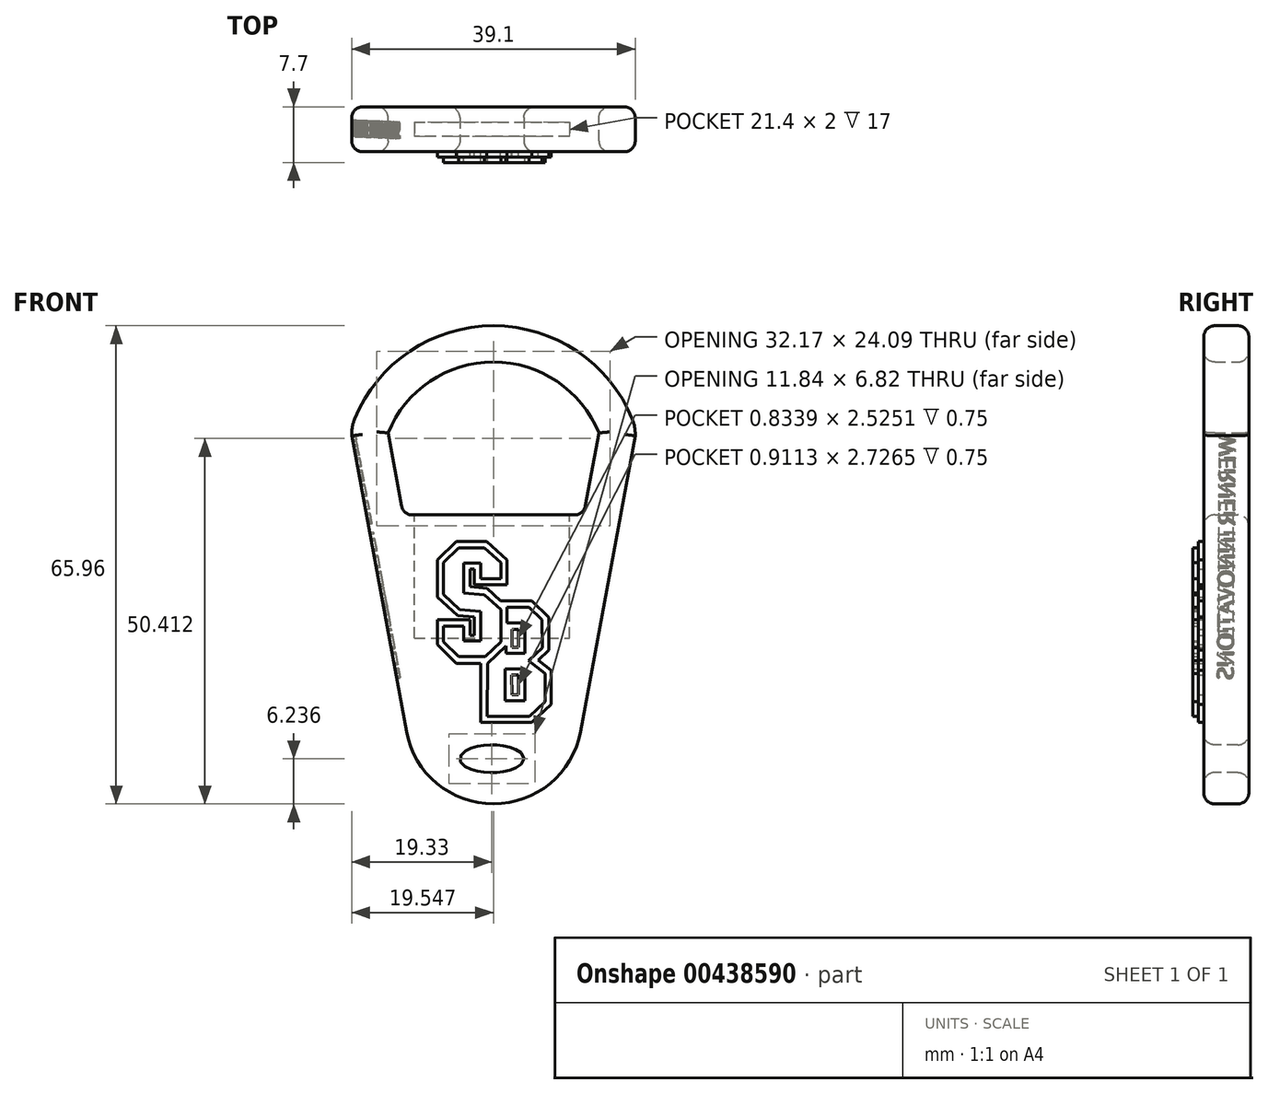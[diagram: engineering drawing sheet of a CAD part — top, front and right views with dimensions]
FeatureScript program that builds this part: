
annotation { "Feature Type Name" : "Feature", "Feature Type Description" : "" }
export const myFeature = defineFeature(function(context is Context, id is Id, definition is map)
    precondition{}
    {
        {
            var Q0;
            Q0=qCreatedBy(makeId("Front.planeOp"),FACE);
            var sketch = newSketch(context, id + "F0", { "sketchPlane" : qUnion([Q0])});
            skLineSegment(sketch, "E0", {"start": v(0.22, 53.5) * mm, "end": v(0.22, -27.22) * mm, "construction": true});
            skLineSegment(sketch, "E1", {"start": v(19.76, 12.33) * mm, "end": v(12.22, -28.48) * mm});
            skLineSegment(sketch, "E2.MirrorCS", {"start": v(-19.33, 12.33) * mm, "end": v(-11.78, -28.48) * mm});
            skLineSegment(sketch, "E3.0", {"start": v(-14.31, 12.71) * mm, "end": v(-12.22, 1.4) * mm});
            skLineSegment(sketch, "E3.3", {"start": v(14.75, 12.71) * mm, "end": v(12.66, 1.4) * mm});
            skLineSegment(sketch, "E4", {"start": v(-12.22, 1.4) * mm, "end": v(12.66, 1.4) * mm});
            skPoint(sketch, "E5", {"position": v(0.22, 20.6) * mm});
            skPoint(sketch, "E6", {"position": v(-14.31, 12.71) * mm});
            skPoint(sketch, "E7.MirrorP", {"position": v(14.75, 12.71) * mm});
            skArc(sketch, "E8", {"start": v(14.75, 12.71) * mm, "mid": v(0.22, 22.5) * mm, "end": v(-14.31, 12.71) * mm});
            skArc(sketch, "E9.0", {"start": v(19.62, 13.97) * mm, "mid": v(0.56, 27.5) * mm, "end": v(-18.94, 14.6) * mm});
            skArc(sketch, "E10", {"start": v(-18.94, 14.6) * mm, "mid": v(-19.26, 13.5) * mm, "end": v(-19.33, 12.33) * mm});
            skArc(sketch, "E11.MirrorCS", {"start": v(19.38, 14.6) * mm, "mid": v(19.7, 13.5) * mm, "end": v(19.76, 12.33) * mm});
            skPoint(sketch, "E12.orphan", {"position": v(-21.9, 26.19) * mm});
            skPoint(sketch, "E13.orphan", {"position": v(22.32, 26.19) * mm});
            skPoint(sketch, "E14.MirrorCS.start.orphan", {"position": v(0.22, 25.6) * mm});
            skArc(sketch, "E15", {"start": v(-11.78, -28.48) * mm, "mid": v(0.22, -38.46) * mm, "end": v(12.22, -28.48) * mm});
            skPoint(sketch, "E16.MirrorCS.end.orphan", {"position": v(0.22, -28.48) * mm});
            skPoint(sketch, "E16.MirrorCS.start.orphan", {"position": v(-11.78, -28.48) * mm});
            skLineSegment(sketch, "E17", {"start": v(-11.78, -28.48) * mm, "end": v(12.22, -28.48) * mm, "construction": true});
            skSolve(sketch);
        }
        {
            var Q0;
            Q0=qSketchRegion(id+"F0",true);
            extrude(context, id + "F1", {"entities" : qUnion([Q0]), "depth" : 6.2 * mm});
        }
        {
            var Q0;
            Q0=makeQuery(id+"F1.opExtrude","CAP_FACE",FACE,{"disambiguationData":[OSD([sQuery(id+"F0.wireOp",EDGE,"E1"),sQuery(id+"F0.wireOp",EDGE,"E2.MirrorCS"),sQuery(id+"F0.wireOp",EDGE,"E3.0"),sQuery(id+"F0.wireOp",EDGE,"E3.3"),sQuery(id+"F0.wireOp",EDGE,"E4"),sQuery(id+"F0.wireOp",EDGE,"E8"),sQuery(id+"F0.wireOp",EDGE,"E9.0"),sQuery(id+"F0.wireOp",EDGE,"E10"),sQuery(id+"F0.wireOp",EDGE,"E11.MirrorCS"),sQuery(id+"F0.wireOp",EDGE,"E15")])],"isStart":false});
            var sketch = newSketch(context, id + "F2", { "sketchPlane" : qUnion([Q0])});
            skEllipse(sketch, "E18", {"center": v(0, -32.22) * mm, "majorRadius": 4.42 * mm, "minorRadius": 1.9 * mm, "majorAxis": v(1, 0)});
            skSolve(sketch);
        }
        {
            var Q0;
            Q0=makeQuery(id+"F2.imprint","IMPRINT",FACE,{"disambiguationData":[TD([[makeQuery(id+"F2.imprint","IMPRINT",EDGE,{"derivedFrom":sQuery(id+"F2.wireOp",EDGE,"E18")}),1.0]])]});
            extrude(context, id + "F3", {"entities" : qUnion([Q0]), "operationType" : NewBodyOperationType.REMOVE, "oppositeDirection" : true, "depth" : 6.5 * mm});
        }
        {
            var Q0;
            Q0=makeQuery(id+"F1.opExtrude","SWEPT_FACE",FACE,{"disambiguationData":[OSD([sQuery(id+"F0.wireOp",EDGE,"E4")])]});
            var sketch = newSketch(context, id + "F4", { "sketchPlane" : qUnion([Q0])});
            skLineSegment(sketch, "E19", {"start": v(0, -2.1) * mm, "end": v(10.7, -2.1) * mm});
            skLineSegment(sketch, "E20.0", {"start": v(0, -4.1) * mm, "end": v(10.7, -4.1) * mm});
            skLineSegment(sketch, "E21", {"start": v(10.7, -2.1) * mm, "end": v(10.7, -4.1) * mm});
            skLineSegment(sketch, "E22", {"start": v(0, -2.1) * mm, "end": v(0, -4.1) * mm, "construction": true});
            skLineSegment(sketch, "E23.MirrorCS", {"start": v(0, -2.1) * mm, "end": v(-10.7, -2.1) * mm});
            skLineSegment(sketch, "E24.MirrorCS", {"start": v(-10.7, -2.1) * mm, "end": v(-10.7, -4.1) * mm});
            skLineSegment(sketch, "E25.MirrorCS", {"start": v(0, -4.1) * mm, "end": v(-10.7, -4.1) * mm});
            skSolve(sketch);
        }
        {
            var Q0;
            Q0=makeQuery(id+"F4.imprint","IMPRINT",FACE,{"disambiguationData":[TD([[makeQuery(id+"F4.imprint","IMPRINT",EDGE,{"derivedFrom":sQuery(id+"F4.wireOp",EDGE,"E19")}),-1.0]])]});
            extrude(context, id + "F5", {"entities" : qUnion([Q0]), "operationType" : NewBodyOperationType.REMOVE, "oppositeDirection" : true, "depth" : 17 * mm});
        }
        {
            var Q0;
            Q0=makeQuery(id+"F1.opExtrude","SWEPT_EDGE",EDGE,{"disambiguationData":[OSD([sQuery(id+"F0.wireOp",EDGE,"E3.0"),sQuery(id+"F0.wireOp",EDGE,"E4")])]});
            var Q1;
            Q1=makeQuery(id+"F1.opExtrude","SWEPT_EDGE",EDGE,{"disambiguationData":[OSD([sQuery(id+"F0.wireOp",EDGE,"E3.3"),sQuery(id+"F0.wireOp",EDGE,"E4")])]});
            var Q2;
            Q2=makeQuery(id+"F1.opExtrude","CAP_FACE",FACE,{"disambiguationData":[OSD([sQuery(id+"F0.wireOp",EDGE,"E1"),sQuery(id+"F0.wireOp",EDGE,"E2.MirrorCS"),sQuery(id+"F0.wireOp",EDGE,"E3.0"),sQuery(id+"F0.wireOp",EDGE,"E3.3"),sQuery(id+"F0.wireOp",EDGE,"E4"),sQuery(id+"F0.wireOp",EDGE,"E8"),sQuery(id+"F0.wireOp",EDGE,"E9.0"),sQuery(id+"F0.wireOp",EDGE,"E10"),sQuery(id+"F0.wireOp",EDGE,"E11.MirrorCS"),sQuery(id+"F0.wireOp",EDGE,"E15")])],"isStart":false});
            var Q3;
            Q3=makeQuery(id+"F1.opExtrude","CAP_FACE",FACE,{"disambiguationData":[OSD([sQuery(id+"F0.wireOp",EDGE,"E1"),sQuery(id+"F0.wireOp",EDGE,"E2.MirrorCS"),sQuery(id+"F0.wireOp",EDGE,"E3.0"),sQuery(id+"F0.wireOp",EDGE,"E3.3"),sQuery(id+"F0.wireOp",EDGE,"E4"),sQuery(id+"F0.wireOp",EDGE,"E8"),sQuery(id+"F0.wireOp",EDGE,"E9.0"),sQuery(id+"F0.wireOp",EDGE,"E10"),sQuery(id+"F0.wireOp",EDGE,"E11.MirrorCS"),sQuery(id+"F0.wireOp",EDGE,"E15")])],"isStart":true});
            fillet(context, id + "F6", {"entities" : qUnion([Q0, Q1, Q2, Q3]), "radius" : 1.5 * mm, "tangentPropagation" : true, "allowEdgeOverflow" : false});
        }
        {
            var Q0;
            Q0=makeQuery(id+"F1.opExtrude","CAP_FACE",FACE,{"disambiguationData":[OSD([sQuery(id+"F0.wireOp",EDGE,"E1"),sQuery(id+"F0.wireOp",EDGE,"E2.MirrorCS"),sQuery(id+"F0.wireOp",EDGE,"E3.0"),sQuery(id+"F0.wireOp",EDGE,"E3.3"),sQuery(id+"F0.wireOp",EDGE,"E4"),sQuery(id+"F0.wireOp",EDGE,"E8"),sQuery(id+"F0.wireOp",EDGE,"E9.0"),sQuery(id+"F0.wireOp",EDGE,"E10"),sQuery(id+"F0.wireOp",EDGE,"E11.MirrorCS"),sQuery(id+"F0.wireOp",EDGE,"E15")])],"isStart":false});
            var sketch = newSketch(context, id + "F7", { "sketchPlane" : qUnion([Q0])});
            skLineSegment(sketch, "E26", {"start": v(-4.9, -2.26) * mm, "end": v(-7.52, -4.8) * mm});
            skLineSegment(sketch, "E27", {"start": v(-7.52, -4.8) * mm, "end": v(-7.52, -9.95) * mm});
            skLineSegment(sketch, "E28", {"start": v(-7.52, -9.95) * mm, "end": v(-4.73, -12.5) * mm});
            skLineSegment(sketch, "E29", {"start": v(-4.73, -12.5) * mm, "end": v(-2.4, -12.68) * mm});
            skLineSegment(sketch, "E30", {"start": v(-2.4, -12.68) * mm, "end": v(-2.4, -15.18) * mm});
            skLineSegment(sketch, "E31", {"start": v(-2.4, -15.18) * mm, "end": v(-3.03, -15.18) * mm});
            skLineSegment(sketch, "E32", {"start": v(-3.03, -15.18) * mm, "end": v(-3.03, -13.07) * mm});
            skLineSegment(sketch, "E33", {"start": v(-3.03, -13.07) * mm, "end": v(-7.52, -13.07) * mm});
            skLineSegment(sketch, "E34", {"start": v(-7.52, -13.07) * mm, "end": v(-7.52, -16.46) * mm});
            skLineSegment(sketch, "E35", {"start": v(-7.52, -16.46) * mm, "end": v(-4.9, -19.07) * mm});
            skLineSegment(sketch, "E36", {"start": v(-4.9, -19.07) * mm, "end": v(-0.61, -19.07) * mm});
            skLineSegment(sketch, "E37", {"start": v(-0.61, -19.07) * mm, "end": v(2.1, -16.52) * mm});
            skLineSegment(sketch, "E38", {"start": v(2.1, -16.52) * mm, "end": v(2.1, -11.34) * mm});
            skLineSegment(sketch, "E39", {"start": v(2.1, -11.34) * mm, "end": v(-0.64, -8.74) * mm});
            skLineSegment(sketch, "E40", {"start": v(-0.64, -8.74) * mm, "end": v(-3, -8.5) * mm});
            skLineSegment(sketch, "E41", {"start": v(-3, -8.5) * mm, "end": v(-3, -6.1) * mm});
            skLineSegment(sketch, "E42", {"start": v(-3, -6.1) * mm, "end": v(-2.4, -6.1) * mm});
            skLineSegment(sketch, "E43", {"start": v(-2.4, -6.1) * mm, "end": v(-2.4, -8.24) * mm});
            skLineSegment(sketch, "E44", {"start": v(-2.4, -8.24) * mm, "end": v(2.1, -8.24) * mm});
            skLineSegment(sketch, "E45", {"start": v(2.1, -8.24) * mm, "end": v(2.1, -4.8) * mm});
            skLineSegment(sketch, "E46", {"start": v(2.1, -4.8) * mm, "end": v(-0.7, -2.26) * mm});
            skLineSegment(sketch, "E47", {"start": v(-0.7, -2.26) * mm, "end": v(-4.9, -2.26) * mm});
            skLineSegment(sketch, "E48", {"start": v(-4.57, -3.13) * mm, "end": v(-6.7, -5.19) * mm});
            skLineSegment(sketch, "E49", {"start": v(-6.7, -5.19) * mm, "end": v(-6.7, -9.58) * mm});
            skLineSegment(sketch, "E50", {"start": v(-6.7, -9.58) * mm, "end": v(-4.44, -11.64) * mm});
            skLineSegment(sketch, "E51", {"start": v(-4.44, -11.64) * mm, "end": v(-1.54, -11.89) * mm});
            skLineSegment(sketch, "E52", {"start": v(-1.54, -11.89) * mm, "end": v(-1.54, -15.99) * mm});
            skLineSegment(sketch, "E53", {"start": v(-1.54, -15.99) * mm, "end": v(-3.92, -15.99) * mm});
            skLineSegment(sketch, "E54", {"start": v(-3.92, -15.99) * mm, "end": v(-3.92, -13.96) * mm});
            skLineSegment(sketch, "E55", {"start": v(-3.92, -13.96) * mm, "end": v(-6.67, -13.96) * mm});
            skLineSegment(sketch, "E56", {"start": v(-6.67, -13.96) * mm, "end": v(-6.67, -16.1) * mm});
            skLineSegment(sketch, "E57", {"start": v(-6.67, -16.1) * mm, "end": v(-4.59, -18.15) * mm});
            skLineSegment(sketch, "E58", {"start": v(-4.59, -18.15) * mm, "end": v(-0.88, -18.15) * mm});
            skLineSegment(sketch, "E59", {"start": v(-0.88, -18.15) * mm, "end": v(1.26, -16.1) * mm});
            skLineSegment(sketch, "E60", {"start": v(1.26, -16.1) * mm, "end": v(1.26, -11.67) * mm});
            skLineSegment(sketch, "E61", {"start": v(1.26, -11.67) * mm, "end": v(-1, -9.6) * mm});
            skLineSegment(sketch, "E62", {"start": v(-1, -9.6) * mm, "end": v(-3.92, -9.34) * mm});
            skLineSegment(sketch, "E63", {"start": v(-3.92, -9.34) * mm, "end": v(-3.92, -5.24) * mm});
            skLineSegment(sketch, "E64", {"start": v(-3.92, -5.24) * mm, "end": v(-1.55, -5.24) * mm});
            skLineSegment(sketch, "E65", {"start": v(-1.55, -5.24) * mm, "end": v(-1.55, -7.4) * mm});
            skLineSegment(sketch, "E66", {"start": v(-1.55, -7.4) * mm, "end": v(1.26, -7.4) * mm});
            skLineSegment(sketch, "E67", {"start": v(1.26, -7.4) * mm, "end": v(1.26, -5.15) * mm});
            skLineSegment(sketch, "E68", {"start": v(1.26, -5.15) * mm, "end": v(-1.04, -3.16) * mm});
            skLineSegment(sketch, "E69", {"start": v(-1.04, -3.16) * mm, "end": v(-4.57, -3.13) * mm});
            skLineSegment(sketch, "E70", {"start": v(1.19, -10.48) * mm, "end": v(5.5, -10.48) * mm});
            skLineSegment(sketch, "E71", {"start": v(5.5, -10.48) * mm, "end": v(7.85, -12.72) * mm});
            skLineSegment(sketch, "E72", {"start": v(7.85, -12.72) * mm, "end": v(7.85, -17.24) * mm});
            skLineSegment(sketch, "E73", {"start": v(7.85, -17.24) * mm, "end": v(6.4, -18.67) * mm});
            skLineSegment(sketch, "E74", {"start": v(6.4, -18.67) * mm, "end": v(8.14, -20.03) * mm});
            skLineSegment(sketch, "E75", {"start": v(8.14, -20.03) * mm, "end": v(8.14, -24.72) * mm});
            skLineSegment(sketch, "E76", {"start": v(8.14, -24.72) * mm, "end": v(5.52, -27.24) * mm});
            skLineSegment(sketch, "E77", {"start": v(5.52, -27.24) * mm, "end": v(-1.56, -27.24) * mm});
            skLineSegment(sketch, "E78", {"start": v(-1.56, -27.24) * mm, "end": v(-1.56, -19.07) * mm});
            skLineSegment(sketch, "E79", {"start": v(2.1, -11.34) * mm, "end": v(5.15, -11.34) * mm});
            skLineSegment(sketch, "E80", {"start": v(5.15, -11.34) * mm, "end": v(6.93, -13.08) * mm});
            skLineSegment(sketch, "E81", {"start": v(6.93, -13.08) * mm, "end": v(6.99, -16.92) * mm});
            skLineSegment(sketch, "E82", {"start": v(6.99, -16.92) * mm, "end": v(5.04, -18.69) * mm});
            skLineSegment(sketch, "E83", {"start": v(5.04, -18.69) * mm, "end": v(7.33, -20.48) * mm});
            skLineSegment(sketch, "E84", {"start": v(7.33, -20.48) * mm, "end": v(7.33, -24.33) * mm});
            skLineSegment(sketch, "E85", {"start": v(7.33, -24.33) * mm, "end": v(5.2, -26.37) * mm});
            skLineSegment(sketch, "E86", {"start": v(5.2, -26.37) * mm, "end": v(-0.63, -26.37) * mm});
            skLineSegment(sketch, "E87", {"start": v(-0.63, -26.37) * mm, "end": v(-0.61, -19.07) * mm});
            skLineSegment(sketch, "E88", {"start": v(1.92, -16.68) * mm, "end": v(1.92, -17.7) * mm});
            skLineSegment(sketch, "E89", {"start": v(1.92, -17.7) * mm, "end": v(4.52, -17.7) * mm});
            skLineSegment(sketch, "E90", {"start": v(4.52, -17.7) * mm, "end": v(4.52, -13.5) * mm});
            skLineSegment(sketch, "E91", {"start": v(4.52, -13.5) * mm, "end": v(2.1, -13.5) * mm});
            skLineSegment(sketch, "E92", {"start": v(2.8, -14.35) * mm, "end": v(2.8, -16.88) * mm});
            skLineSegment(sketch, "E93", {"start": v(2.8, -16.88) * mm, "end": v(3.64, -16.88) * mm});
            skLineSegment(sketch, "E94", {"start": v(3.64, -16.88) * mm, "end": v(3.64, -14.35) * mm});
            skLineSegment(sketch, "E95", {"start": v(2.8, -14.35) * mm, "end": v(3.64, -14.35) * mm});
            skLineSegment(sketch, "E96", {"start": v(1.88, -19.85) * mm, "end": v(4.52, -19.85) * mm});
            skLineSegment(sketch, "E97", {"start": v(4.52, -19.85) * mm, "end": v(4.52, -24.24) * mm});
            skLineSegment(sketch, "E98", {"start": v(4.52, -24.24) * mm, "end": v(1.84, -24.24) * mm});
            skLineSegment(sketch, "E99", {"start": v(1.84, -24.24) * mm, "end": v(1.84, -19.85) * mm});
            skLineSegment(sketch, "E100", {"start": v(1.84, -19.85) * mm, "end": v(1.89, -19.85) * mm});
            skLineSegment(sketch, "E101", {"start": v(2.74, -20.7) * mm, "end": v(3.65, -20.7) * mm});
            skLineSegment(sketch, "E102", {"start": v(3.65, -20.7) * mm, "end": v(3.65, -23.42) * mm});
            skLineSegment(sketch, "E103", {"start": v(3.65, -23.42) * mm, "end": v(2.75, -23.42) * mm});
            skLineSegment(sketch, "E104", {"start": v(2.75, -23.42) * mm, "end": v(2.74, -20.7) * mm});
            skSolve(sketch);
        }
        {
            var Q0;
            Q0=makeQuery(id+"F7.imprint","IMPRINT",FACE,{"disambiguationData":[TD([[makeQuery(id+"F7.imprint","IMPRINT",EDGE,{"derivedFrom":sQuery(id+"F7.wireOp",EDGE,"E48")}),1.0]])]});
            var Q1;
            {var subQ0=sQuery(id+"F7.wireOp",EDGE,"E79");Q1=makeQuery(id+"F7.imprint","IMPRINT",FACE,{"disambiguationData":[TD([[makeQuery(id+"F7.imprint","IMPRINT",EDGE,{"derivedFrom":subQ0}),-1.0]])]});}
            extrude(context, id + "F8", {"entities" : qUnion([Q0, Q1]), "operationType" : NewBodyOperationType.ADD, "depth" : 1.5 * mm});
        }
        {
            var Q0;
            Q0=makeQuery(id+"F7.imprint","IMPRINT",FACE,{"disambiguationData":[TD([[makeQuery(id+"F7.imprint","IMPRINT",EDGE,{"derivedFrom":sQuery(id+"F7.wireOp",EDGE,"E26")}),1.0]])]});
            var Q1;
            {var subQ0=sQuery(id+"F7.wireOp",EDGE,"E88");Q1=makeQuery(id+"F7.imprint","IMPRINT",FACE,{"disambiguationData":[TD([[makeQuery(id+"F7.imprint","IMPRINT",EDGE,{"derivedFrom":subQ0}),1.0]])]});}
            var Q2;
            {var subQ1=sQuery(id+"F7.wireOp",EDGE,"E96");Q2=makeQuery(id+"F7.imprint","IMPRINT",FACE,{"disambiguationData":[TD([[makeQuery(id+"F7.imprint","IMPRINT",EDGE,{"derivedFrom":subQ1}),-1.0]])]});}
            var Q3;
            {var subQ4=sQuery(id+"F7.wireOp",EDGE,"E70");Q3=makeQuery(id+"F7.imprint","IMPRINT",FACE,{"disambiguationData":[TD([[makeQuery(id+"F7.imprint","IMPRINT",EDGE,{"derivedFrom":subQ4}),-1.0]])]});}
            extrude(context, id + "F9", {"entities" : qUnion([Q0, Q1, Q2, Q3]), "operationType" : NewBodyOperationType.ADD, "depth" : .75 * mm});
        }
        {
            var Q0;
            Q0=makeQuery(id+"F1.opExtrude","SWEPT_FACE",FACE,{"disambiguationData":[OSD([sQuery(id+"F0.wireOp",EDGE,"E2.MirrorCS")])]});
            var sketch = newSketch(context, id + "F10", { "sketchPlane" : qUnion([Q0])});
            skText(sketch, "E105", { "text": "WERNER INNOVATIONS", "fontName": "OpenSans-Regular.ttf"});
            const initialGuessF10  = {"E105": [0.00187, 0.01563, 0.00753, -0.99997, 0.00224]};
            skSetInitialGuess(sketch, initialGuessF10);
            skSolve(sketch);
        }
        {
            var Q0;
            Q0 = qSketchRegion(id + "F10", true);
            extrude(context, id + "F11", {"entities" : qUnion([Q0]), "operationType" : NewBodyOperationType.REMOVE, "oppositeDirection" : true, "depth" : .5 * mm});
        }
    });
